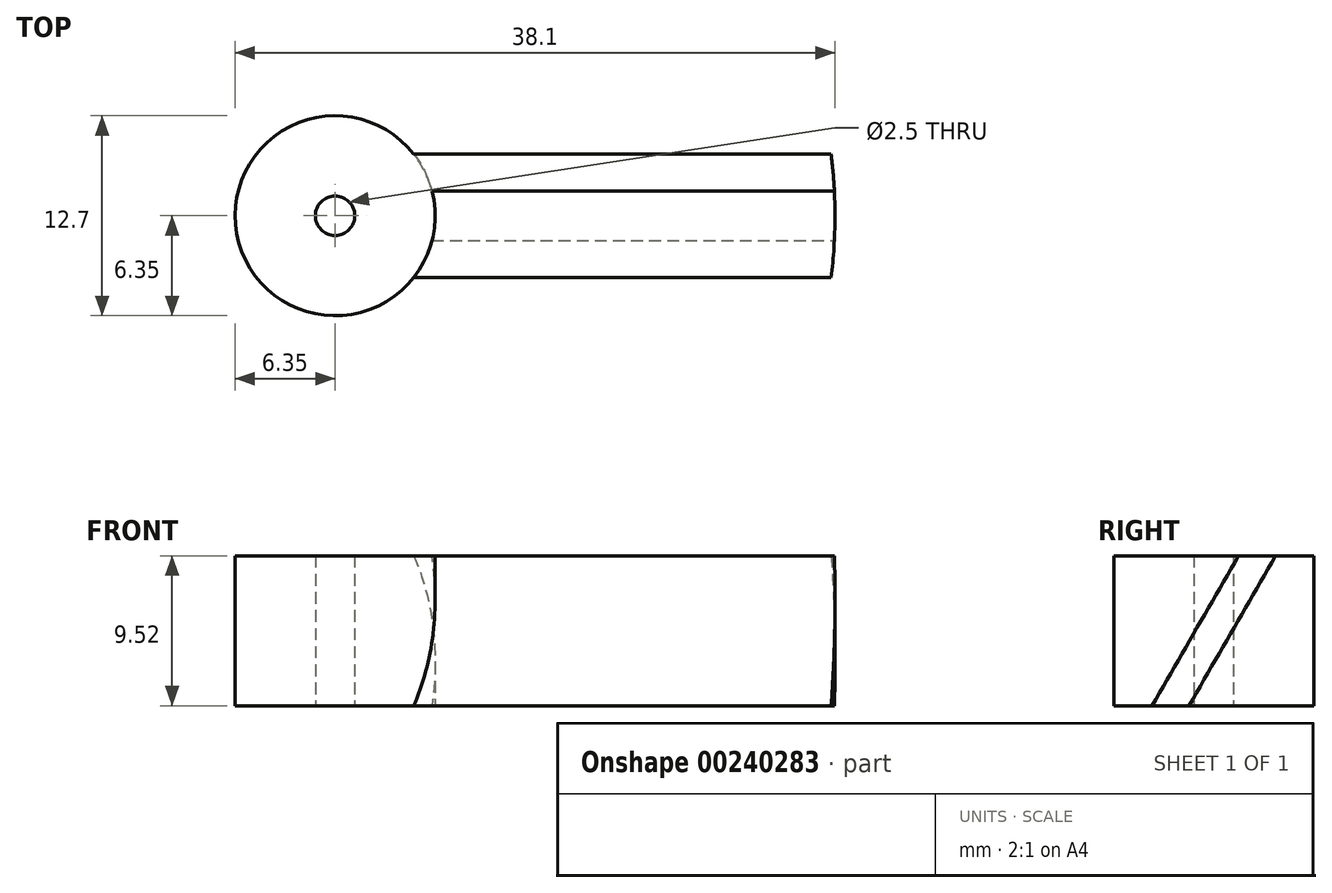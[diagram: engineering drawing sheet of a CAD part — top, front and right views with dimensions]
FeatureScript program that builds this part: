
annotation { "Feature Type Name" : "Feature", "Feature Type Description" : "" }
export const myFeature = defineFeature(function(context is Context, id is Id, definition is map)
    precondition{}
    {
        {
            var Q0;
            Q0=qCreatedBy(makeId("Top.planeOp"),FACE);
            var sketch = newSketch(context, id + "F0", { "sketchPlane" : qUnion([Q0])});
            skCircle(sketch, "E0", {"center": v(0, 0) * mm, "radius": 6.35 * mm});
            skCircle(sketch, "E1", {"center": v(0, 0) * mm, "radius": 1.25 * mm});
            skSolve(sketch);
        }
        {
            var Q0;
            Q0 = qSketchRegion(id + "F0", true);
            extrude(context, id + "F1", {"entities" : qUnion([Q0]), "endBound" : BoundingType.SYMMETRIC, "depth" : 9.52 * mm});
        }
        {
            var Q0;
            Q0=qCreatedBy(makeId("Right.planeOp"),FACE);
            cPlane(context, id + "F2", {"entities" : qUnion([Q0]), "cplaneType" : CPlaneType.OFFSET, "offset" : 152.4 * mm, "width" : 152.4 * mm, "height" : 152.4 * mm});
        }
        {
            var Q0;
            Q0=qCreatedBy(id+"F2.planeOp",FACE);
            var sketch = newSketch(context, id + "F3", { "sketchPlane" : qUnion([Q0])});
            skLineSegment(sketch, "E2", {"start": v(2.75, 4.76) * mm, "end": v(-2.75, -4.76) * mm, "construction": true});
            skLineSegment(sketch, "E3", {"start": v(-3.92, -4.76) * mm, "end": v(-1.58, -4.76) * mm});
            skLineSegment(sketch, "E4", {"start": v(-1.58, -4.76) * mm, "end": v(3.92, 4.76) * mm});
            skLineSegment(sketch, "E5", {"start": v(3.92, 4.76) * mm, "end": v(1.58, 4.76) * mm});
            skLineSegment(sketch, "E6", {"start": v(1.58, 4.76) * mm, "end": v(-3.92, -4.76) * mm});
            skSolve(sketch);
        }
        {
            var Q0;
            Q0=makeQuery(id+"F3.imprint","IMPRINT",FACE,{"disambiguationData":[TD([[makeQuery(id+"F3.imprint","IMPRINT",EDGE,{"derivedFrom":sQuery(id+"F3.wireOp",EDGE,"E3")}),1.0]])]});
            var Q1;
            Q1=makeQuery(id+"F1.opExtrude","SWEPT_BODY",BODY,{"disambiguationData":[OSD([sQuery(id+"F0.wireOp",EDGE,"E0"),sQuery(id+"F0.wireOp",EDGE,"E1")])]});
            extrude(context, id + "F4", {"entities" : qUnion([Q0]), "operationType" : NewBodyOperationType.ADD, "endBound" : BoundingType.UP_TO_BODY, "oppositeDirection" : true, "endBoundEntityBody" : qUnion([Q1]), "depth" : 25.4 * mm});
        }
        {
            var Q0;
            {var subQ0=sQuery(id+"F3.wireOp",EDGE,"E5");Q0=makeQuery(id+"Fv9mXGDykzdbgjw_1.5.F4.boolean.opBoolean","MERGE",FACE,{"derivedFrom":[makeQuery(id+"Fv9mXGDykzdbgjw_1.4.F4.boolean.opBoolean","MERGE",FACE,{"derivedFrom":[makeQuery(id+"Fv9mXGDykzdbgjw_1.3.F4.boolean.opBoolean","MERGE",FACE,{"derivedFrom":[makeQuery(id+"Fv9mXGDykzdbgjw_1.2.F4.boolean.opBoolean","MERGE",FACE,{"derivedFrom":[makeQuery(id+"Fv9mXGDykzdbgjw_1.1.F4.boolean.opBoolean","MERGE",FACE,{"derivedFrom":[makeQuery(id+"F4.boolean.opBoolean","MERGE",FACE,{"derivedFrom":[makeQuery(id+"F1.opExtrude","CAP_FACE",FACE,{"disambiguationData":[OSD([sQuery(id+"F0.wireOp",EDGE,"E0"),sQuery(id+"F0.wireOp",EDGE,"E1")])],"isStart":false}),makeQuery(id+"F4.opExtrude","SWEPT_FACE",FACE,{"disambiguationData":[OSD([subQ0])]})]}),makeQuery(id+"Fv9mXGDykzdbgjw_1.1.F4.opExtrude","SWEPT_FACE",FACE,{"disambiguationData":[OSD([subQ0])]})]}),makeQuery(id+"Fv9mXGDykzdbgjw_1.2.F4.opExtrude","SWEPT_FACE",FACE,{"disambiguationData":[OSD([subQ0])]})]}),makeQuery(id+"Fv9mXGDykzdbgjw_1.3.F4.opExtrude","SWEPT_FACE",FACE,{"disambiguationData":[OSD([subQ0])]})]}),makeQuery(id+"Fv9mXGDykzdbgjw_1.4.F4.opExtrude","SWEPT_FACE",FACE,{"disambiguationData":[OSD([subQ0])]})]}),makeQuery(id+"Fv9mXGDykzdbgjw_1.5.F4.opExtrude","SWEPT_FACE",FACE,{"disambiguationData":[OSD([subQ0])]})]});}
            var sketch = newSketch(context, id + "F5", { "sketchPlane" : qUnion([Q0])});
            skCircle(sketch, "E7", {"center": v(0, 0) * mm, "radius": 31.75 * mm});
            skCircle(sketch, "E8", {"center": v(0, 0) * mm, "radius": 254 * mm});
            skSolve(sketch);
        }
        {
            var Q0;
            Q0 = qSketchRegion(id + "F5", true);
            extrude(context, id + "F6", {"entities" : qUnion([Q0]), "operationType" : NewBodyOperationType.REMOVE, "endBound" : BoundingType.THROUGH_ALL, "oppositeDirection" : true, "depth" : 25.4 * mm});
        }
    });
